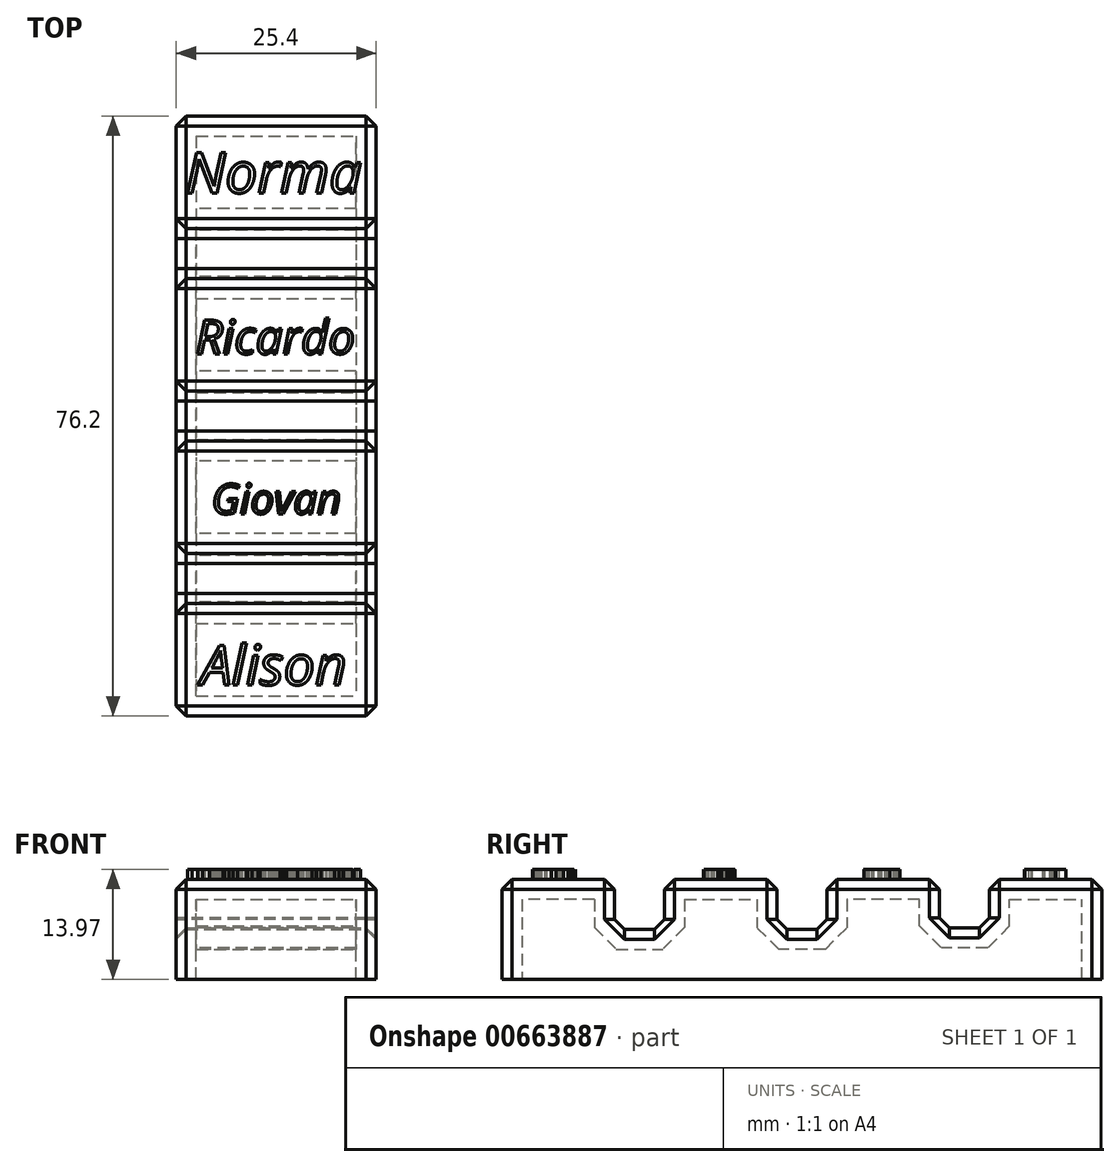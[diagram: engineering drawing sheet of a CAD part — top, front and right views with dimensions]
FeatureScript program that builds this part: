
annotation { "Feature Type Name" : "Feature", "Feature Type Description" : "" }
export const myFeature = defineFeature(function(context is Context, id is Id, definition is map)
    precondition{}
    {
        {
            var Q0;
            Q0=qCreatedBy(makeId("Top.planeOp"),FACE);
            var sketch = newSketch(context, id + "F0", { "sketchPlane" : qUnion([Q0])});
            skLineSegment(sketch, "E0.bottom", {"start": v(-38.1, -12.7) * mm, "end": v(38.1, -12.7) * mm});
            skLineSegment(sketch, "E0.top", {"start": v(-38.1, 12.7) * mm, "end": v(38.1, 12.7) * mm});
            skLineSegment(sketch, "E0.left", {"start": v(-38.1, -12.7) * mm, "end": v(-38.1, 12.7) * mm});
            skLineSegment(sketch, "E0.right", {"start": v(38.1, -12.7) * mm, "end": v(38.1, 12.7) * mm});
            skPoint(sketch, "E0.middle", {"position": v(0, 0) * mm});
            skSolve(sketch);
        }
        {
            var Q0;
            Q0 = qSketchRegion(id + "F0", true);
            extrude(context, id + "F1", {"entities" : qUnion([Q0]), "depth" : 12.7 * mm, "offsetDistance" : 25.4 * mm});
        }
        {
            var Q0;
            Q0=makeQuery(id+"F1.opExtrude","SWEPT_FACE",FACE,{"disambiguationData":[OSD([sQuery(id+"F0.wireOp",EDGE,"E0.bottom")])]});
            var sketch = newSketch(context, id + "F2", { "sketchPlane" : qUnion([Q0])});
            skLineSegment(sketch, "E1", {"start": v(-38.1, 6.35) * mm, "end": v(38.1, 6.35) * mm, "construction": true});
            skLineSegment(sketch, "E2.bottom", {"start": v(3.18, 6.35) * mm, "end": v(-3.17, 6.35) * mm});
            skLineSegment(sketch, "E2.top", {"start": v(3.18, 19.05) * mm, "end": v(-3.17, 19.05) * mm});
            skLineSegment(sketch, "E2.left", {"start": v(3.18, 6.35) * mm, "end": v(3.18, 19.05) * mm});
            skLineSegment(sketch, "E2.right", {"start": v(-3.17, 6.35) * mm, "end": v(-3.17, 19.05) * mm});
            skPoint(sketch, "E2.middle", {"position": v(0, 12.7) * mm});
            skLineSegment(sketch, "E3.bottom", {"start": v(-17.48, 18.84) * mm, "end": v(-23.83, 18.84) * mm});
            skLineSegment(sketch, "E3.top", {"start": v(-17.48, 6.56) * mm, "end": v(-23.83, 6.56) * mm});
            skLineSegment(sketch, "E3.left", {"start": v(-17.48, 18.84) * mm, "end": v(-17.48, 6.56) * mm});
            skLineSegment(sketch, "E3.right", {"start": v(-23.83, 18.84) * mm, "end": v(-23.83, 6.56) * mm});
            skPoint(sketch, "E3.middle", {"position": v(-20.65, 12.7) * mm});
            skLineSegment(sketch, "E4.bottom", {"start": v(23.83, 19.02) * mm, "end": v(17.48, 19.02) * mm});
            skLineSegment(sketch, "E4.top", {"start": v(23.83, 6.38) * mm, "end": v(17.48, 6.38) * mm});
            skLineSegment(sketch, "E4.left", {"start": v(23.83, 19.02) * mm, "end": v(23.83, 6.38) * mm});
            skLineSegment(sketch, "E4.right", {"start": v(17.48, 19.02) * mm, "end": v(17.48, 6.38) * mm});
            skPoint(sketch, "E4.middle", {"position": v(20.65, 12.7) * mm});
            skSolve(sketch);
        }
        {
            var Q0;
            Q0 = qSketchRegion(id + "F2", true);
            extrude(context, id + "F3", {"entities" : qUnion([Q0]), "operationType" : NewBodyOperationType.REMOVE, "endBound" : BoundingType.THROUGH_ALL, "oppositeDirection" : true, "depth" : 25.4 * mm, "offsetDistance" : 25.4 * mm});
        }
        {
            var Q0;
            {var subQ0=sQuery(id+"F0.wireOp",EDGE,"E0.bottom");var subQ1=sQuery(id+"F0.wireOp",EDGE,"E0.right");var subQ2=sQuery(id+"F0.wireOp",EDGE,"E0.top");Q0=makeQuery(id+"F3.boolean.opBoolean","SPLIT",FACE,{"disambiguationData":[TD([makeQuery(id+"F1.opExtrude","SWEPT_FACE",FACE,{"disambiguationData":[OSD([subQ1])]})])],"derivedFrom":makeQuery(id+"F1.opExtrude","CAP_FACE",FACE,{"disambiguationData":[OSD([subQ0,subQ2,sQuery(id+"F0.wireOp",EDGE,"E0.left"),subQ1])],"isStart":false})});}
            var Q1;
            {var subQ0=sQuery(id+"F0.wireOp",EDGE,"E0.bottom");var subQ1=sQuery(id+"F0.wireOp",EDGE,"E0.top");Q1=makeQuery(id+"F3.boolean.opBoolean","SPLIT",FACE,{"disambiguationData":[TD([makeQuery(id+"F3.opExtrude","SWEPT_FACE",FACE,{"disambiguationData":[OSD([sQuery(id+"F2.wireOp",EDGE,"E2.left")])]})])],"derivedFrom":makeQuery(id+"F1.opExtrude","CAP_FACE",FACE,{"disambiguationData":[OSD([subQ0,subQ1,sQuery(id+"F0.wireOp",EDGE,"E0.left"),sQuery(id+"F0.wireOp",EDGE,"E0.right")])],"isStart":false})});}
            var Q2;
            {var subQ0=sQuery(id+"F0.wireOp",EDGE,"E0.bottom");var subQ1=sQuery(id+"F0.wireOp",EDGE,"E0.top");Q2=makeQuery(id+"F3.boolean.opBoolean","SPLIT",FACE,{"disambiguationData":[TD([makeQuery(id+"F3.opExtrude","SWEPT_FACE",FACE,{"disambiguationData":[OSD([sQuery(id+"F2.wireOp",EDGE,"E2.right")])]})])],"derivedFrom":makeQuery(id+"F1.opExtrude","CAP_FACE",FACE,{"disambiguationData":[OSD([subQ0,subQ1,sQuery(id+"F0.wireOp",EDGE,"E0.left"),sQuery(id+"F0.wireOp",EDGE,"E0.right")])],"isStart":false})});}
            var Q3;
            {var subQ0=sQuery(id+"F0.wireOp",EDGE,"E0.bottom");var subQ1=sQuery(id+"F0.wireOp",EDGE,"E0.top");var subQ2=sQuery(id+"F0.wireOp",EDGE,"E0.left");Q3=makeQuery(id+"F3.boolean.opBoolean","SPLIT",FACE,{"disambiguationData":[TD([makeQuery(id+"F1.opExtrude","SWEPT_FACE",FACE,{"disambiguationData":[OSD([subQ2])]})])],"derivedFrom":makeQuery(id+"F1.opExtrude","CAP_FACE",FACE,{"disambiguationData":[OSD([subQ0,subQ1,subQ2,sQuery(id+"F0.wireOp",EDGE,"E0.right")])],"isStart":false})});}
            var Q4;
            Q4=makeQuery(id+"F3.boolean.opBoolean","COPY",FACE,{"derivedFrom":makeQuery(id+"F3.opExtrude","SWEPT_FACE",FACE,{"disambiguationData":[OSD([sQuery(id+"F2.wireOp",EDGE,"E3.top")])]})});
            var Q5;
            Q5=makeQuery(id+"F3.boolean.opBoolean","COPY",FACE,{"derivedFrom":makeQuery(id+"F3.opExtrude","SWEPT_FACE",FACE,{"disambiguationData":[OSD([sQuery(id+"F2.wireOp",EDGE,"E2.bottom")])]})});
            var Q6;
            Q6=makeQuery(id+"F3.boolean.opBoolean","COPY",FACE,{"derivedFrom":makeQuery(id+"F3.opExtrude","SWEPT_FACE",FACE,{"disambiguationData":[OSD([sQuery(id+"F2.wireOp",EDGE,"E4.top")])]})});
            var Q7;
            Q7=makeQuery(id+"F1.opExtrude","SWEPT_EDGE",EDGE,{"disambiguationData":[OSD([sQuery(id+"F0.wireOp",EDGE,"E0.bottom"),sQuery(id+"F0.wireOp",EDGE,"E0.right")])]});
            var Q8;
            Q8=makeQuery(id+"F1.opExtrude","SWEPT_EDGE",EDGE,{"disambiguationData":[OSD([sQuery(id+"F0.wireOp",EDGE,"E0.bottom"),sQuery(id+"F0.wireOp",EDGE,"E0.left")])]});
            var Q9;
            Q9=makeQuery(id+"F1.opExtrude","SWEPT_EDGE",EDGE,{"disambiguationData":[OSD([sQuery(id+"F0.wireOp",EDGE,"E0.top"),sQuery(id+"F0.wireOp",EDGE,"E0.right")])]});
            var Q10;
            Q10=makeQuery(id+"F1.opExtrude","SWEPT_EDGE",EDGE,{"disambiguationData":[OSD([sQuery(id+"F0.wireOp",EDGE,"E0.top"),sQuery(id+"F0.wireOp",EDGE,"E0.left")])]});
            chamfer(context, id + "F4", {"entities" : qUnion([Q0, Q1, Q2, Q3, Q4, Q5, Q6, Q7, Q8, Q9, Q10]), "width" : 1.27 * mm, "tangentPropagation" : true});
        }
        {
            var Q0;
            Q0=makeQuery(id+"F1.opExtrude","CAP_FACE",FACE,{"disambiguationData":[OSD([sQuery(id+"F0.wireOp",EDGE,"E0.bottom"),sQuery(id+"F0.wireOp",EDGE,"E0.top"),sQuery(id+"F0.wireOp",EDGE,"E0.left"),sQuery(id+"F0.wireOp",EDGE,"E0.right")])],"isStart":true});
            shell(context, id + "F5", {"entities" : qUnion([Q0]), "thickness" : 2.54 * mm});
        }
        {
            var Q0;
            Q0=makeQuery(id+"F1.opExtrude","SWEPT_BODY",BODY,{"disambiguationData":[OSD([sQuery(id+"F0.wireOp",EDGE,"E0.bottom"),sQuery(id+"F0.wireOp",EDGE,"E0.top"),sQuery(id+"F0.wireOp",EDGE,"E0.left"),sQuery(id+"F0.wireOp",EDGE,"E0.right")])]});
            var Q1;
            {var subQ0=sQuery(id+"F0.wireOp",EDGE,"E0.right");Q1=makeQuery(id+"F4.opChamfer","BLEND_EDGE",EDGE,{"blendedFrom":[makeQuery(id+"F1.opExtrude","SWEPT_EDGE",EDGE,{"disambiguationData":[OSD([sQuery(id+"F0.wireOp",EDGE,"E0.bottom"),subQ0])]}),makeQuery(id+"F1.opExtrude","SWEPT_FACE",FACE,{"disambiguationData":[OSD([subQ0])]})],"blendedInto":[makeQuery(id+"F1.opExtrude","SWEPT_FACE",FACE,{"disambiguationData":[OSD([subQ0])]})]});}
            transform(context, id + "F6", {"entities" : qUnion([Q0]), "transformType" : TransformType.ROTATION, "transformAxis" : qUnion([Q1]), "angle" : 90 * degree, "makeCopy" : false});
        }
        {
            var Q0;
            {var subQ0=sQuery(id+"F0.wireOp",EDGE,"E0.bottom");var subQ1=sQuery(id+"F0.wireOp",EDGE,"E0.right");var subQ2=sQuery(id+"F0.wireOp",EDGE,"E0.top");Q0=makeQuery(id+"F3.boolean.opBoolean","SPLIT",FACE,{"disambiguationData":[TD([makeQuery(id+"F1.opExtrude","SWEPT_FACE",FACE,{"disambiguationData":[OSD([subQ1])]})])],"derivedFrom":makeQuery(id+"F1.opExtrude","CAP_FACE",FACE,{"disambiguationData":[OSD([subQ0,subQ2,sQuery(id+"F0.wireOp",EDGE,"E0.left"),subQ1])],"isStart":false})});}
            var sketch = newSketch(context, id + "F7", { "sketchPlane" : qUnion([Q0])});
            skText(sketch, "E5", { "text": "Alison", "fontName": "OpenSans-Italic.ttf"});
            const initialGuessF7  = {"E5": [0.03996, -0.0075, 1, 0, 0.00508]};
            skSetInitialGuess(sketch, initialGuessF7);
            skSolve(sketch);
        }
        {
            var Q0;
            Q0 = qSketchRegion(id + "F7", true);
            extrude(context, id + "F8", {"entities" : qUnion([Q0]), "operationType" : NewBodyOperationType.ADD, "depth" : 1.27 * mm, "offsetDistance" : 25.4 * mm});
        }
        {
            var Q0;
            {var subQ0=sQuery(id+"F0.wireOp",EDGE,"E0.bottom");var subQ1=sQuery(id+"F0.wireOp",EDGE,"E0.top");Q0=makeQuery(id+"F3.boolean.opBoolean","SPLIT",FACE,{"disambiguationData":[TD([makeQuery(id+"F3.opExtrude","SWEPT_FACE",FACE,{"disambiguationData":[OSD([sQuery(id+"F2.wireOp",EDGE,"E2.right")])]})])],"derivedFrom":makeQuery(id+"F1.opExtrude","CAP_FACE",FACE,{"disambiguationData":[OSD([subQ0,subQ1,sQuery(id+"F0.wireOp",EDGE,"E0.left"),sQuery(id+"F0.wireOp",EDGE,"E0.right")])],"isStart":false})});}
            var sketch = newSketch(context, id + "F9", { "sketchPlane" : qUnion([Q0])});
            skText(sketch, "E6", { "text": "Ricardo ", "fontName": "OpenSans-Italic.ttf"});
            const initialGuessF9  = {"E6": [0.0393, 0.03455, 1, 0, 0.00432]};
            skSetInitialGuess(sketch, initialGuessF9);
            skSolve(sketch);
        }
        {
            var Q0;
            Q0 = qSketchRegion(id + "F9", true);
            extrude(context, id + "F10", {"entities" : qUnion([Q0]), "operationType" : NewBodyOperationType.ADD, "depth" : 1.27 * mm, "offsetDistance" : 25.4 * mm});
        }
        {
            var Q0;
            {var subQ0=sQuery(id+"F0.wireOp",EDGE,"E0.bottom");var subQ1=sQuery(id+"F0.wireOp",EDGE,"E0.top");Q0=makeQuery(id+"F3.boolean.opBoolean","SPLIT",FACE,{"disambiguationData":[TD([makeQuery(id+"F3.opExtrude","SWEPT_FACE",FACE,{"disambiguationData":[OSD([sQuery(id+"F2.wireOp",EDGE,"E2.left")])]})])],"derivedFrom":makeQuery(id+"F1.opExtrude","CAP_FACE",FACE,{"disambiguationData":[OSD([subQ0,subQ1,sQuery(id+"F0.wireOp",EDGE,"E0.left"),sQuery(id+"F0.wireOp",EDGE,"E0.right")])],"isStart":false})});}
            var sketch = newSketch(context, id + "F11", { "sketchPlane" : qUnion([Q0])});
            skText(sketch, "E7", { "text": "Giovan", "fontName": "OpenSans-Italic.ttf"});
            const initialGuessF11  = {"E7": [0.04132, 0.01423, 1, 0, 0.00383]};
            skSetInitialGuess(sketch, initialGuessF11);
            skSolve(sketch);
        }
        {
            var Q0;
            Q0 = qSketchRegion(id + "F11", true);
            extrude(context, id + "F12", {"entities" : qUnion([Q0]), "operationType" : NewBodyOperationType.ADD, "depth" : 1.27 * mm, "offsetDistance" : 25.4 * mm});
        }
        {
            var Q0;
            {var subQ0=sQuery(id+"F0.wireOp",EDGE,"E0.bottom");var subQ1=sQuery(id+"F0.wireOp",EDGE,"E0.top");var subQ2=sQuery(id+"F0.wireOp",EDGE,"E0.left");Q0=makeQuery(id+"F3.boolean.opBoolean","SPLIT",FACE,{"disambiguationData":[TD([makeQuery(id+"F1.opExtrude","SWEPT_FACE",FACE,{"disambiguationData":[OSD([subQ2])]})])],"derivedFrom":makeQuery(id+"F1.opExtrude","CAP_FACE",FACE,{"disambiguationData":[OSD([subQ0,subQ1,subQ2,sQuery(id+"F0.wireOp",EDGE,"E0.right")])],"isStart":false})});}
            var sketch = newSketch(context, id + "F13", { "sketchPlane" : qUnion([Q0])});
            skText(sketch, "E8", { "text": "Norma", "fontName": "OpenSans-Italic.ttf"});
            const initialGuessF13  = {"E8": [0.038, 0.055, 1, 0, 0.0052]};
            skSetInitialGuess(sketch, initialGuessF13);
            skSolve(sketch);
        }
        {
            var Q0;
            Q0 = qSketchRegion(id + "F13", true);
            extrude(context, id + "F14", {"entities" : qUnion([Q0]), "operationType" : NewBodyOperationType.ADD, "depth" : 1.27 * mm, "offsetDistance" : 25.4 * mm});
        }
    });
